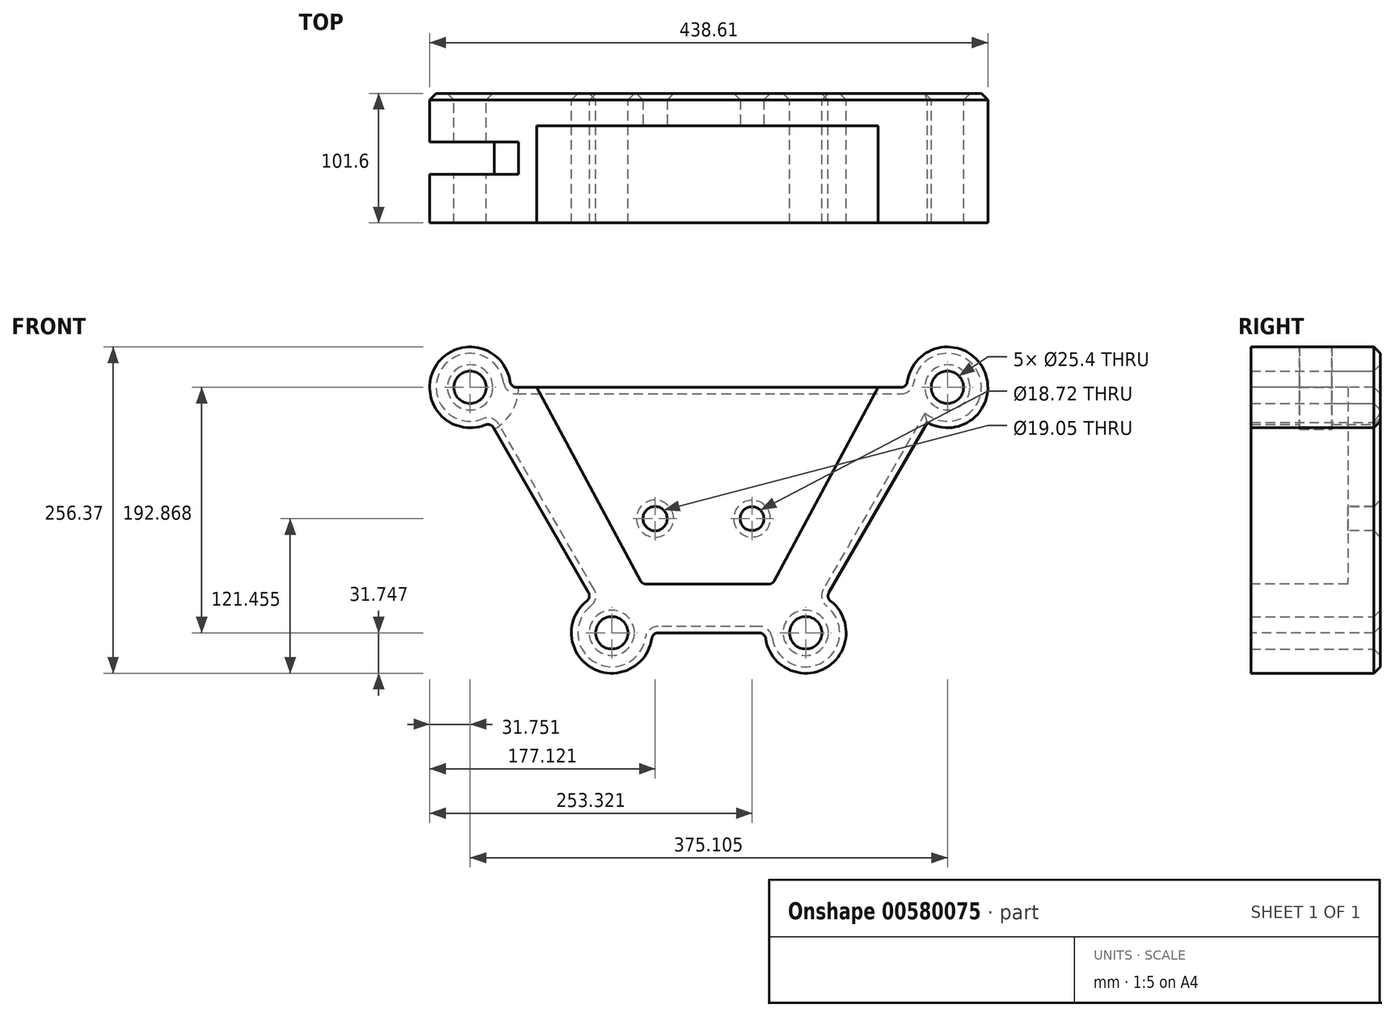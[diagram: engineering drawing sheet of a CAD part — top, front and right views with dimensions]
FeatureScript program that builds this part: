
annotation { "Feature Type Name" : "Feature", "Feature Type Description" : "" }
export const myFeature = defineFeature(function(context is Context, id is Id, definition is map)
    precondition{}
    {
        {
            var Q0;
            Q0=qCreatedBy(makeId("Front.planeOp"),FACE);
            var sketch = newSketch(context, id + "F0", { "sketchPlane" : qUnion([Q0])});
            skLineSegment(sketch, "E0", {"start": v(-60.59, -93.03) * mm, "end": v(91.81, -93.03) * mm});
            skLineSegment(sketch, "E1", {"start": v(91.81, -93.03) * mm, "end": v(203.17, 99.84) * mm});
            skLineSegment(sketch, "E2", {"start": v(203.17, 99.84) * mm, "end": v(-171.94, 99.84) * mm});
            skLineSegment(sketch, "E3", {"start": v(-171.94, 99.84) * mm, "end": v(-60.59, -93.03) * mm});
            skCircle(sketch, "E4", {"center": v(-171.94, 99.84) * mm, "radius": 12.7 * mm});
            skCircle(sketch, "E5", {"center": v(-171.94, 99.84) * mm, "radius": 31.75 * mm});
            skCircle(sketch, "E6", {"center": v(203.17, 99.84) * mm, "radius": 12.7 * mm});
            skCircle(sketch, "E7", {"center": v(203.17, 99.84) * mm, "radius": 31.75 * mm});
            skCircle(sketch, "E8", {"center": v(91.81, -93.03) * mm, "radius": 31.75 * mm});
            skCircle(sketch, "E9", {"center": v(-60.59, -93.03) * mm, "radius": 12.7 * mm});
            skCircle(sketch, "E10", {"center": v(-60.59, -93.03) * mm, "radius": 31.75 * mm});
            skCircle(sketch, "E11", {"center": v(91.81, -93.03) * mm, "radius": 12.7 * mm});
            skSolve(sketch);
        }
        {
            var Q0;
            Q0 = qSketchRegion(id + "F0", true);
            extrude(context, id + "F1", {"entities" : qUnion([Q0]), "endBound" : BoundingType.SYMMETRIC, "depth" : 101.6 * mm, "offsetDistance" : 25.4 * mm});
        }
        {
            var Q0;
            Q0=makeQuery(id+"F1.opExtrude","CAP_FACE",FACE,{"disambiguationData":[OSD([sQuery(id+"F0.wireOp",EDGE,"E0"),sQuery(id+"F0.wireOp",EDGE,"E1"),sQuery(id+"F0.wireOp",EDGE,"E2"),sQuery(id+"F0.wireOp",EDGE,"E3"),sQuery(id+"F0.wireOp",EDGE,"E4"),sQuery(id+"F0.wireOp",EDGE,"E5"),sQuery(id+"F0.wireOp",EDGE,"E6"),sQuery(id+"F0.wireOp",EDGE,"E7"),sQuery(id+"F0.wireOp",EDGE,"E8"),sQuery(id+"F0.wireOp",EDGE,"E9"),sQuery(id+"F0.wireOp",EDGE,"E10"),sQuery(id+"F0.wireOp",EDGE,"E11")])],"isStart":false});
            var sketch = newSketch(context, id + "F2", { "sketchPlane" : qUnion([Q0])});
            skLineSegment(sketch, "E12", {"start": v(-119.62, 99.84) * mm, "end": v(-36.53, -54.8) * mm});
            skLineSegment(sketch, "E13", {"start": v(-36.53, -54.8) * mm, "end": v(65.61, -54.8) * mm});
            skLineSegment(sketch, "E14", {"start": v(65.61, -54.8) * mm, "end": v(148.7, 99.84) * mm});
            skLineSegment(sketch, "E15", {"start": v(148.7, 99.84) * mm, "end": v(-119.62, 99.84) * mm});
            skSolve(sketch);
        }
        {
            var Q0;
            Q0 = qSketchRegion(id + "F2", true);
            extrude(context, id + "F3", {"entities" : qUnion([Q0]), "operationType" : NewBodyOperationType.REMOVE, "oppositeDirection" : true, "depth" : 76.2 * mm, "offsetDistance" : 25.4 * mm});
        }
        {
            var Q0;
            Q0=qCreatedBy(makeId("Front.planeOp"),FACE);
            var sketch = newSketch(context, id + "F4", { "sketchPlane" : qUnion([Q0])});
            skCircle(sketch, "E16", {"center": v(-171.96, 99.88) * mm, "radius": 38.1 * mm});
            skCircle(sketch, "E17", {"center": v(203.24, 99.92) * mm, "radius": 38.1 * mm});
            skCircle(sketch, "E18", {"center": v(91.68, -93.01) * mm, "radius": 38.1 * mm});
            skCircle(sketch, "E19", {"center": v(-60.64, -92.99) * mm, "radius": 38.1 * mm});
            skSolve(sketch);
        }
        {
            var Q0;
            Q0=qCreatedBy(makeId("Front.planeOp"),FACE);
            var sketch = newSketch(context, id + "F5", { "sketchPlane" : qUnion([Q0])});
            skCircle(sketch, "E20", {"center": v(-26.57, -3.32) * mm, "radius": 9.53 * mm});
            skCircle(sketch, "E21", {"center": v(49.63, -3.32) * mm, "radius": 9.36 * mm});
            skLineSegment(sketch, "E22", {"start": v(-26.57, -3.32) * mm, "end": v(49.63, -3.32) * mm, "construction": true});
            skLineSegment(sketch, "E23", {"start": v(11.53, -3.32) * mm, "end": v(11.53, -53.87) * mm, "construction": true});
            skSolve(sketch);
        }
        {
            var Q0;
            Q0 = qSketchRegion(id + "F5", true);
            extrude(context, id + "F6", {"entities" : qUnion([Q0]), "operationType" : NewBodyOperationType.REMOVE, "oppositeDirection" : true, "depth" : 93.73 * mm, "offsetDistance" : 25.4 * mm});
        }
        {
            var Q0;
            Q0=makeQuery(id+"F4.imprint","IMPRINT",FACE,{"disambiguationData":[TD([[makeQuery(id+"F4.imprint","IMPRINT",EDGE,{"derivedFrom":sQuery(id+"F4.wireOp",EDGE,"E16")}),1.0]])]});
            extrude(context, id + "F7", {"entities" : qUnion([Q0]), "operationType" : NewBodyOperationType.REMOVE, "endBound" : BoundingType.SYMMETRIC, "depth" : 25.4 * mm, "offsetDistance" : 25.4 * mm});
        }
        {
            var Q0;
            {var subQ0=sQuery(id+"F0.wireOp",EDGE,"E5");var subQ1=sQuery(id+"F0.wireOp",EDGE,"E2");Q0=makeQuery(id+"F7.boolean.opBoolean","SPLIT",EDGE,{"disambiguationData":[TD([makeQuery(id+"F7.opExtrude","CAP_FACE",FACE,{"disambiguationData":[OSD([sQuery(id+"F4.wireOp",EDGE,"E16")])],"isStart":true})])],"derivedFrom":makeQuery(id+"F1.opExtrude","SWEPT_EDGE",EDGE,{"disambiguationData":[OSD([subQ1,subQ0])]})});}
            var Q1;
            {var subQ0=sQuery(id+"F0.wireOp",EDGE,"E5");var subQ1=sQuery(id+"F0.wireOp",EDGE,"E2");Q1=makeQuery(id+"F7.boolean.opBoolean","SPLIT",EDGE,{"disambiguationData":[TD([makeQuery(id+"F7.opExtrude","CAP_FACE",FACE,{"disambiguationData":[OSD([sQuery(id+"F4.wireOp",EDGE,"E16")])],"isStart":false})])],"derivedFrom":makeQuery(id+"F1.opExtrude","SWEPT_EDGE",EDGE,{"disambiguationData":[OSD([subQ1,subQ0])]})});}
            var Q2;
            Q2=makeQuery(id+"F1.opExtrude","SWEPT_EDGE",EDGE,{"disambiguationData":[OSD([sQuery(id+"F0.wireOp",EDGE,"E2"),sQuery(id+"F0.wireOp",EDGE,"E7")])]});
            var Q3;
            Q3=makeQuery(id+"F1.opExtrude","SWEPT_EDGE",EDGE,{"disambiguationData":[OSD([sQuery(id+"F0.wireOp",EDGE,"E0"),sQuery(id+"F0.wireOp",EDGE,"E8")])]});
            var Q4;
            Q4=makeQuery(id+"F1.opExtrude","SWEPT_EDGE",EDGE,{"disambiguationData":[OSD([sQuery(id+"F0.wireOp",EDGE,"E0"),sQuery(id+"F0.wireOp",EDGE,"E10")])]});
            var Q5;
            Q5=makeQuery(id+"F1.opExtrude","SWEPT_EDGE",EDGE,{"disambiguationData":[OSD([sQuery(id+"F0.wireOp",EDGE,"E1"),sQuery(id+"F0.wireOp",EDGE,"E8")])]});
            var Q6;
            Q6=makeQuery(id+"F1.opExtrude","SWEPT_EDGE",EDGE,{"disambiguationData":[OSD([sQuery(id+"F0.wireOp",EDGE,"E3"),sQuery(id+"F0.wireOp",EDGE,"E10")])]});
            var Q7;
            {var subQ0=sQuery(id+"F0.wireOp",EDGE,"E5");var subQ1=sQuery(id+"F0.wireOp",EDGE,"E3");Q7=makeQuery(id+"F7.boolean.opBoolean","SPLIT",EDGE,{"disambiguationData":[TD([makeQuery(id+"F7.opExtrude","CAP_FACE",FACE,{"disambiguationData":[OSD([sQuery(id+"F4.wireOp",EDGE,"E16")])],"isStart":true})])],"derivedFrom":makeQuery(id+"F1.opExtrude","SWEPT_EDGE",EDGE,{"disambiguationData":[OSD([subQ1,subQ0])]})});}
            var Q8;
            {var subQ0=sQuery(id+"F0.wireOp",EDGE,"E5");var subQ1=sQuery(id+"F0.wireOp",EDGE,"E3");Q8=makeQuery(id+"F7.boolean.opBoolean","SPLIT",EDGE,{"disambiguationData":[TD([makeQuery(id+"F7.opExtrude","CAP_FACE",FACE,{"disambiguationData":[OSD([sQuery(id+"F4.wireOp",EDGE,"E16")])],"isStart":false})])],"derivedFrom":makeQuery(id+"F1.opExtrude","SWEPT_EDGE",EDGE,{"disambiguationData":[OSD([subQ1,subQ0])]})});}
            var Q9;
            Q9=makeQuery(id+"F3.boolean.opBoolean","COPY",EDGE,{"derivedFrom":makeQuery(id+"F3.opExtrude","SWEPT_EDGE",EDGE,{"disambiguationData":[OSD([sQuery(id+"F0.wireOp",EDGE,"E2"),sQuery(id+"F2.wireOp",EDGE,"E14"),sQuery(id+"F2.wireOp",EDGE,"E15")])]})});
            var Q10;
            Q10=makeQuery(id+"F3.boolean.opBoolean","COPY",EDGE,{"derivedFrom":makeQuery(id+"F3.opExtrude","SWEPT_EDGE",EDGE,{"disambiguationData":[OSD([sQuery(id+"F0.wireOp",EDGE,"E2"),sQuery(id+"F2.wireOp",EDGE,"E12"),sQuery(id+"F2.wireOp",EDGE,"E15")])]})});
            var Q11;
            Q11=makeQuery(id+"F3.boolean.opBoolean","COPY",EDGE,{"derivedFrom":makeQuery(id+"F3.opExtrude","SWEPT_EDGE",EDGE,{"disambiguationData":[OSD([sQuery(id+"F2.wireOp",EDGE,"E12"),sQuery(id+"F2.wireOp",EDGE,"E13")])]})});
            var Q12;
            Q12=makeQuery(id+"F3.boolean.opBoolean","COPY",EDGE,{"derivedFrom":makeQuery(id+"F3.opExtrude","SWEPT_EDGE",EDGE,{"disambiguationData":[OSD([sQuery(id+"F2.wireOp",EDGE,"E13"),sQuery(id+"F2.wireOp",EDGE,"E14")])]})});
            fillet(context, id + "F8", {"entities" : qUnion([Q0, Q1, Q2, Q3, Q4, Q5, Q6, Q7, Q8, Q9, Q10, Q11, Q12]), "radius" : 5.08 * mm, "tangentPropagation" : true, "allowEdgeOverflow" : false});
        }
        {
            var Q0;
            Q0=makeQuery(id+"F3.boolean.opBoolean","COPY",EDGE,{"derivedFrom":makeQuery(id+"F3.opExtrude","CAP_EDGE",EDGE,{"disambiguationData":[OSD([sQuery(id+"F2.wireOp",EDGE,"E15")])],"isStart":false})});
            var Q1;
            Q1=makeQuery(id+"F3.boolean.opBoolean","COPY",EDGE,{"derivedFrom":makeQuery(id+"F3.opExtrude","CAP_EDGE",EDGE,{"disambiguationData":[OSD([sQuery(id+"F2.wireOp",EDGE,"E14")])],"isStart":true})});
            var Q2;
            Q2=makeQuery(id+"F3.boolean.opBoolean","COPY",EDGE,{"derivedFrom":makeQuery(id+"F3.opExtrude","CAP_EDGE",EDGE,{"disambiguationData":[OSD([sQuery(id+"F2.wireOp",EDGE,"E12")])],"isStart":true})});
            var Q3;
            Q3=makeQuery(id+"F1.opExtrude","CAP_FACE",FACE,{"disambiguationData":[OSD([sQuery(id+"F0.wireOp",EDGE,"E0"),sQuery(id+"F0.wireOp",EDGE,"E1"),sQuery(id+"F0.wireOp",EDGE,"E2"),sQuery(id+"F0.wireOp",EDGE,"E3"),sQuery(id+"F0.wireOp",EDGE,"E4"),sQuery(id+"F0.wireOp",EDGE,"E5"),sQuery(id+"F0.wireOp",EDGE,"E6"),sQuery(id+"F0.wireOp",EDGE,"E7"),sQuery(id+"F0.wireOp",EDGE,"E8"),sQuery(id+"F0.wireOp",EDGE,"E9"),sQuery(id+"F0.wireOp",EDGE,"E10"),sQuery(id+"F0.wireOp",EDGE,"E11")])],"isStart":true});
            chamfer(context, id + "F9", {"entities" : qUnion([Q0, Q1, Q2, Q3]), "width" : 5.08 * mm, "tangentPropagation" : true});
        }
    });
